# Revit family: NAU_Naughtone_Tbls_Sweep_AFTERQA
name_source: partatom
category: Furniture
units: mm (PartAtom-declared; Revit-internal decimal feet)

## family parameters
Always vertical = Yes
Cut with Voids When Loaded = No
OmniClass Number = 23.40.20.00
OmniClass Title = General Furniture and Specialties
Room Calculation Point = No
Shared = No
Work Plane-Based = No

## types (5) — shared parameters
Assembly Code = E2020
AssetType = Movable
BIMObjectName = NAU_Naughtone_Tables_Sweep
Category = Pr_40_50_21 : Desks, tables and worktops
Color = Black base. White MFMDF top
DurationUnit = year
Features = Legs available in 16 different RALs. Tops available in Black or White MFMDF, or Oak or Walnut Veneer with matching edge band.
Finish = Base is powdercoated steel in RAL 9005 black
IfcExportAs = IfcFurnishingElementType
IfcExportType = TABLE
ManufacturerName = Naughtone
ManufacturerURL = www.naughtone.com
Material = Legs in steel. Top in MFMDF or Veneered MDF
NBSDescription = Tables
NBSReference = 45-35-86/327
Name = Tables_Sweep_Naughtone
NominalHeight = 350 mm  [stored 1.14829 ft]
ProductInformation = https://www.naughtone.com
URL = https://www.naughtone.com
Uniclass2015Code = Pr_40_50_21
Uniclass2015Title = Desks, tables and worktops
Uniclass2015Version = Products v1.26
Version = 1
WarrantyDescription = Request warranty information from naughtone
WarrantyDurationLabor = 10
WarrantyDurationParts = 10
WarrantyDurationUnit = year
zero-valued in all types: Default Elevation, NumberOfChairs, WorksurfaceArea

## per-type parameters (varying)
| type | CircleLegRadius | IsCircularTableTop | IsSquareTableTop | ModelNumber | ModelReference | NominalLength | NominalWidth | Radius | Shape | Size | TableTopRadius |
| Sweep Coffee Table 550 Square | 263 mm | No | Yes | NOSWP550S | Sweep Coffee Table 550 Square | 550 mm | 550 mm | 250 mm  [stored 0.82021 ft] | Square | 550 x 550 x 350mm | 275 mm |
| Sweep Coffee Table 750 Square | 363 mm | No | Yes | NOSWP750S | Sweep Coffee Table 750 Square | 750 mm  [stored 2.46063 ft] | 750 mm  [stored 2.46063 ft] | 350 mm  [stored 1.14829 ft] | Square | 750 x 750 x 350mm | 375 mm  [stored 1.23031 ft] |
| Sweep Coffee Table 650 Diameter | 313 mm | Yes | No | NOSWP650D | Sweep Coffee Table 650 Diameter | 650 mm  [stored 2.13255 ft] | 650 mm  [stored 2.13255 ft] | 300 mm | Circular | 650 x  650 x 350mm | 325 mm  [stored 1.06627 ft] |
| Sweep Coffee Table 850 Diameter | 413 mm | Yes | No | NOSWP850D | Sweep Coffee Table 850 Diameter | 850 mm  [stored 2.78871 ft] | 850 mm  [stored 2.78871 ft] | 400 mm  [stored 1.31234 ft] | Circular | 850 x 850 x 350mm | 425 mm  [stored 1.39436 ft] |
| Sweep Coffee Table 900 x 550 Rectangle | 438 mm | No | Yes | NOSWP955R | Sweep Coffee Table 900x550 Rectangle | 900 mm  [stored 2.95276 ft] | 550 mm | 425 mm  [stored 1.39436 ft] | Rectangle | 900 x 550 x 350mm | 450 mm  [stored 1.47638 ft] |

note: [stored X ft] marks values corroborated as IEEE doubles in the binary element streams (Revit-internal decimal feet)

## geometry (parser evidence)
native form markers: Sweep x77
no freeform markers — native parametric forms only
